# Revit family: Gewindestifte
name_source: partatom
category: HLS-Bauteile
revit_build: Autodesk Revit 2018 (Build: 20190510_1515(x64)
units: mm (PartAtom-declared; Revit-internal decimal feet)

## family parameters
Arbeitsebenenbasiert = Ja
Beim Laden mit Abzugskörper schneiden = Nein
Bemaßung runder Anschluss = Durchmesser verwenden
Gemeinsam genutzt = Ja
Immer vertikal = Nein
Raumberechnungspunkt = Nein
Teiletyp = Normal

## types (28) — shared parameters
Firma = MEFA Befestigungs- und Montagesysteme GmbH
Vorgabe-Ansicht = 1219 mm

## per-type parameters (varying)
| type | Artikelnummer | D | EAN | Fabrikat | Festigkeitsklasse | Gewicht | Gewicht pro Bauteil | Gewinde | Kurztext1 | Kurztext2 | L | Länge | Länge Gewinde 1 | Material | Mengeneinheit | Oberflaeche | vpe |
| Gewindestift M 8x 20 | 0730815 | 7 mm  [stored 0.0229659 ft] | 4250928416575 | MEFA | 4.6 | 0.01 kg | 0.01 kg | M8 | Gewindestift DIN 976-1 | M8 x 20 mm gvz FK 4.6 | 20 mm  [stored 0.0656168 ft] | 20 mm  [stored 0.0656168 ft] | 20 mm | Stahl | St | galvanisch verzinkt | 100 |
| Gewindestift M 8x 30 | 0730823 | 7 mm  [stored 0.0229659 ft] | 4250928416582 | MEFA | 4.6 | 0.01 kg | 0.01 kg | M8 | Gewindestift DIN 976-1 | M8 x 30 mm gvz FK 4.6 | 30 mm  [stored 0.0984252 ft] | 30 mm  [stored 0.0984252 ft] | 30 mm | Stahl | St | galvanisch verzinkt | 100 |
| Gewindestift M 8x 35 | 0731358 | 7 mm  [stored 0.0229659 ft] | 4250928416797 | MEFA | 4.6 | 0.01 kg | 0.01 kg | M8 | Gewindestift DIN 976-1 | M8 x 35 mm gvz FK 4.6 | 35 mm  [stored 0.114829 ft] | 35 mm  [stored 0.114829 ft] | 35 mm | Stahl | St | galvanisch verzinkt | 100 |
| Gewindestift M 8x 40 | 0730831 | 7 mm  [stored 0.0229659 ft] | 4250928416599 | MEFA | 4.6 | 0.01 kg | 0.01 kg | M8 | Gewindestift DIN 976-1 | M8 x 40 mm gvz FK 4.6 | 40 mm  [stored 0.131234 ft] | 40 mm  [stored 0.131234 ft] | 40 mm | Stahl | St | galvanisch verzinkt | 100 |
| Gewindestift M 8x 50 | 0730858 | 7 mm  [stored 0.0229659 ft] | 4250928416605 | MEFA | 4.6 | 0.02 kg | 0.02 kg | M8 | Gewindestift DIN 976-1 | M8 x 50 mm gvz FK 4.6 | 50 mm  [stored 0.164042 ft] | 50 mm  [stored 0.164042 ft] | 50 mm | Stahl | St | galvanisch verzinkt | 100 |
| Gewindestift M 8x 70 | 0730874 | 7 mm  [stored 0.0229659 ft] | 4250928416612 | MEFA | 4.6 | 0.02 kg | 0.02 kg | M8 | Gewindestift DIN 976-1 | M8 x 70 mm gvz FK 4.6 | 70 mm  [stored 0.229659 ft] | 70 mm  [stored 0.229659 ft] | 70 mm | Stahl | St | galvanisch verzinkt | 100 |
| Gewindestift M 8x 90 | 0730890 | 7 mm  [stored 0.0229659 ft] | 4250928416629 | MEFA | 4.6 | 0.03 kg | 0.03 kg | M8 | Gewindestift DIN 976-1 | M8 x 90 mm gvz FK 4.6 | 90 mm  [stored 0.295276 ft] | 90 mm  [stored 0.295276 ft] | 90 mm | Stahl | St | galvanisch verzinkt | 100 |
| Gewindestift M 8x110 | 0730912 | 7 mm  [stored 0.0229659 ft] | 4250928416636 | MEFA | 4.6 | 0.04 kg | 0.04 kg | M8 | Gewindestift DIN 976-1 | M8 x 110 mm gvz FK 4.6 | 110 mm  [stored 0.360892 ft] | 110 mm  [stored 0.360892 ft] | 110 mm | Stahl | St | galvanisch verzinkt | 100 |
| Gewindestift M 8x140 | 0730940 | 7 mm  [stored 0.0229659 ft] | 4250928416643 | MEFA | 4.6 | 0.05 kg | 0.05 kg | M8 | Gewindestift DIN 976-1 | M8 x 140 mm gvz FK 4.6 | 140 mm  [stored 0.459318 ft] | 140 mm  [stored 0.459318 ft] | 140 mm | Stahl | St | galvanisch verzinkt | 100 |
| Gewindestift M 8x160 | 0730963 | 7 mm  [stored 0.0229659 ft] | 4250928416650 | MEFA | 4.6 | 0.05 kg | 0.05 kg | M8 | Gewindestift DIN 976-1 | M8 x 160 mm gvz FK 4.6 | 160 mm  [stored 0.524934 ft] | 160 mm  [stored 0.524934 ft] | 160 mm | Stahl | St | galvanisch verzinkt | 100 |
| Gewindestift M10x 20 | 0731021 | 8 mm  [stored 0.0262467 ft] | 4250928416667 | MEFA | 4.6 | 0.01 kg | 0.01 kg | M10 | Gewindestift DIN 976-1 | M10 x 20 mm gvz FK 4.6 | 20 mm  [stored 0.0656168 ft] | 20 mm  [stored 0.0656168 ft] | 20 mm | Stahl | St | galvanisch verzinkt | 100 |
| Gewindestift M10x 25 | 0731032 | 8 mm  [stored 0.0262467 ft] | 4250928416674 | MEFA | 4.6 | 0.01 kg | 0.01 kg | M10 | Gewindestift DIN 976-1 | M10 x 25 mm gvz FK 4.6 | 25 mm  [stored 0.082021 ft] | 25 mm  [stored 0.082021 ft] | 25 mm | Stahl | St | galvanisch verzinkt | 100 |
| Gewindestift M10x 30 | 0731048 | 8 mm  [stored 0.0262467 ft] | 4250928416681 | MEFA | 4.6 | 0.02 kg | 0.02 kg | M10 | Gewindestift DIN 976-1 | M10 x 30 mm gvz FK 4.6 | 30 mm  [stored 0.0984252 ft] | 30 mm  [stored 0.0984252 ft] | 30 mm | Stahl | St | galvanisch verzinkt | 100 |
| Gewindestift M10x 35 | 0733350 | 8 mm  [stored 0.0262467 ft] | 4250928416926 | MEFA | 4.6 | 0.02 kg | 0.02 kg | M10 | Gewindestift DIN 976-1 | M10 x 35 mm gvz FK 4.6 | 35 mm  [stored 0.114829 ft] | 35 mm  [stored 0.114829 ft] | 35 mm | Stahl | St | galvanisch verzinkt | 100 |
| Gewindestift M10x 40 | 0731056 | 8 mm  [stored 0.0262467 ft] | 4250928416698 | MEFA | 4.6 | 0.02 kg | 0.02 kg | M10 | Gewindestift DIN 976-1 | M10 x 40 mm gvz FK 4.6 | 40 mm  [stored 0.131234 ft] | 40 mm  [stored 0.131234 ft] | 40 mm | Stahl | St | galvanisch verzinkt | 100 |
| Gewindestift M10x 50 | 0731064 | 8 mm  [stored 0.0262467 ft] | 4250928416704 | MEFA | 4.6 | 0.03 kg | 0.03 kg | M10 | Gewindestift DIN 976-1 | M10 x 50 mm gvz FK 4.6 | 50 mm  [stored 0.164042 ft] | 50 mm  [stored 0.164042 ft] | 50 mm | Stahl | St | galvanisch verzinkt | 100 |
| Gewindestift M10x 70 | 0731072 | 8 mm  [stored 0.0262467 ft] | 4250928416711 | MEFA | 4.6 | 0.04 kg | 0.04 kg | M10 | Gewindestift DIN 976-1 | M10 x 70 mm gvz FK 4.6 | 70 mm  [stored 0.229659 ft] | 70 mm  [stored 0.229659 ft] | 70 mm | Stahl | St | galvanisch verzinkt | 100 |
| Gewindestift M10x 90 | 0731099 | 8 mm  [stored 0.0262467 ft] | 4250928416728 | MEFA | 4.6 | 0.05 kg | 0.05 kg | M10 | Gewindestift DIN 976-1 | M10 x 90 mm gvz FK 4.6 | 90 mm  [stored 0.295276 ft] | 90 mm  [stored 0.295276 ft] | 90 mm | Stahl | St | galvanisch verzinkt | 100 |
| Gewindestift M10x110 | 0731110 | 8 mm  [stored 0.0262467 ft] | 4250928416735 | MEFA | 4.6 | 0.06 kg | 0.06 kg | M10 | Gewindestift DIN 976-1 | M10 x 110 mm gvz FK 4.6 | 110 mm  [stored 0.360892 ft] | 110 mm  [stored 0.360892 ft] | 110 mm | Stahl | St | galvanisch verzinkt | 50 |
| Gewindestift M12x 35 | 0731234 | 10 mm  [stored 0.0328084 ft] | 4250928416742 | MEFA | 4.6 | 0.03 kg | 0.03 kg | M12 | Gewindestift DIN 976-1 | M12 x 35 mm gvz FK 4.6 | 35 mm  [stored 0.114829 ft] | 35 mm  [stored 0.114829 ft] | 35 mm | Stahl | St | galvanisch verzinkt | 50 |
| Gewindestift M12x 50 | 0731250 | 10 mm  [stored 0.0328084 ft] | 4250928416759 | MEFA | 4.6 | 0.04 kg | 0.04 kg | M12 | Gewindestift DIN 976-1 | M12 x 50 mm gvz FK 4.6 | 50 mm  [stored 0.164042 ft] | 50 mm  [stored 0.164042 ft] | 50 mm | Stahl | St | galvanisch verzinkt | 50 |
| Gewindestift M12x 70 | 0731269 | 10 mm  [stored 0.0328084 ft] | 4250928416766 | MEFA | 4.6 | 0.05 kg | 0.05 kg | M12 | Gewindestift DIN 976-1 | M12 x 70 mm gvz FK 4.6 | 70 mm  [stored 0.229659 ft] | 70 mm  [stored 0.229659 ft] | 70 mm | Stahl | St | galvanisch verzinkt | 50 |
| Gewindestift M12x 90 | 0731293 | 10 mm  [stored 0.0328084 ft] | 4250928416773 | MEFA | 4.6 | 0.07 kg | 0.07 kg | M12 | Gewindestift DIN 976-1 | M12 x 90 mm gvz FK 4.6 | 90 mm  [stored 0.295276 ft] | 90 mm  [stored 0.295276 ft] | 90 mm | Stahl | St | galvanisch verzinkt | 50 |
| Gewindestift M12x110 | 0731315 | 10 mm  [stored 0.0328084 ft] | 4250928416780 | MEFA | 4.6 | 0.08 kg | 0.08 kg | M12 | Gewindestift DIN 976-1 | M12 x 110 mm gvz FK 4.6 | 110 mm  [stored 0.360892 ft] | 110 mm  [stored 0.360892 ft] | 110 mm | Stahl | St | galvanisch verzinkt | 50 |
| Gewindestift M16x 70 | 0731672 | 14 mm  [stored 0.0459318 ft] | 4250928416803 | MEFA | 4.6 | 0.09 kg | 0.09 kg | M16 | Gewindestift DIN 976-1 | M16 x 70 mm gvz FK 4.6 | 70 mm  [stored 0.229659 ft] | 70 mm  [stored 0.229659 ft] | 70 mm | Stahl | St | galvanisch verzinkt | 25 |
| Gewindestift M16x110 | 0731715 | 14 mm  [stored 0.0459318 ft] | 4250928416810 | MEFA | 4.6 | 0.14 kg | 0.14 kg | M16 | Gewindestift DIN 976-1 | M16 x 110 mm gvz FK 4.6 | 110 mm  [stored 0.360892 ft] | 110 mm  [stored 0.360892 ft] | 110 mm | Stahl | St | galvanisch verzinkt | 25 |
| Gewindestift M16x160 | 0731763 | 14 mm  [stored 0.0459318 ft] | 4250928416827 | MEFA | 4.6 | 0.21 kg | 0.21 kg | M16 | Gewindestift DIN 976-1 | M16 x 160 mm gvz FK 4.6 | 160 mm  [stored 0.524934 ft] | 160 mm  [stored 0.524934 ft] | 160 mm | Stahl | St | galvanisch verzinkt | 25 |
| Gewindestift M12x 40 | 0731240 | 10 mm  [stored 0.0328084 ft] |  |  |  | 0.03 kg | 0.03 kg |  |  |  | 40 mm  [stored 0.131234 ft] | 0 mm  [stored 0 ft] |  |  |  |  |  |

note: [stored X ft] marks values corroborated as IEEE doubles in the binary element streams (Revit-internal decimal feet)
